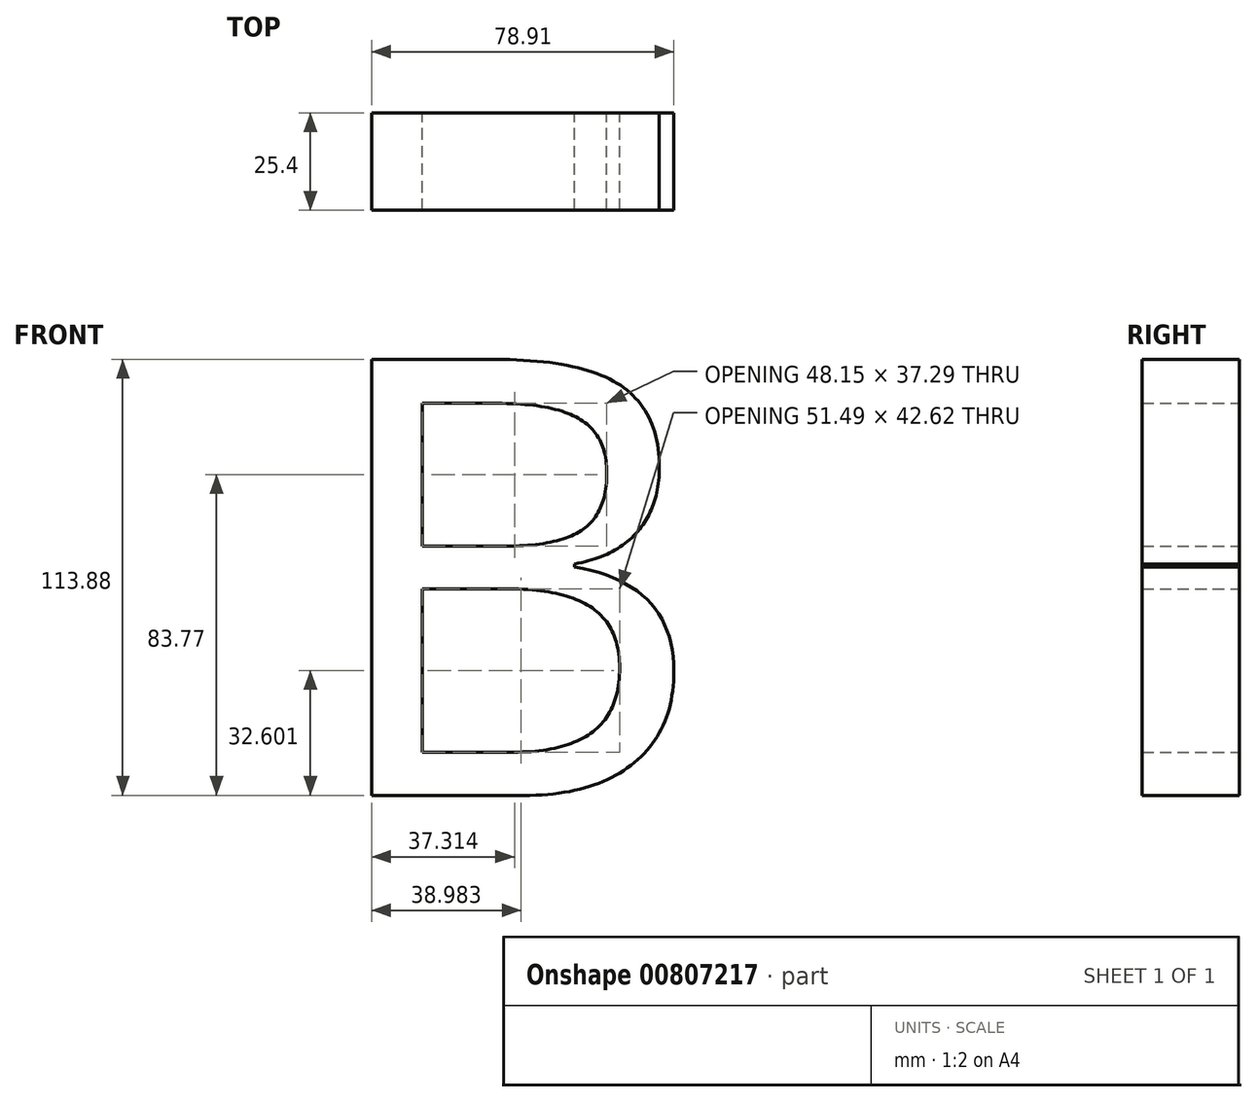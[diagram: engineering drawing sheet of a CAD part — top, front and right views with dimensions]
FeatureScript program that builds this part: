
annotation { "Feature Type Name" : "Feature", "Feature Type Description" : "" }
export const myFeature = defineFeature(function(context is Context, id is Id, definition is map)
    precondition{}
    {
        {
            var Q0;
            Q0=qCreatedBy(makeId("Front.planeOp"),FACE);
            var sketch = newSketch(context, id + "F0", { "sketchPlane" : qUnion([Q0])});
            skText(sketch, "E0", { "text": "B", "fontName": "OpenSans-Regular.ttf"});
            const initialGuessF0  = {"E0": [-0.04743, -0.0576, 1, 0, 0.11485]};
            skSetInitialGuess(sketch, initialGuessF0);
            skSolve(sketch);
        }
        {
            var Q0;
            Q0 = qSketchRegion(id + "F0", true);
            extrude(context, id + "F1", {"entities" : qUnion([Q0]), "depth" : 25.4 * mm, "offsetDistance" : 25.4 * mm});
        }
    });
